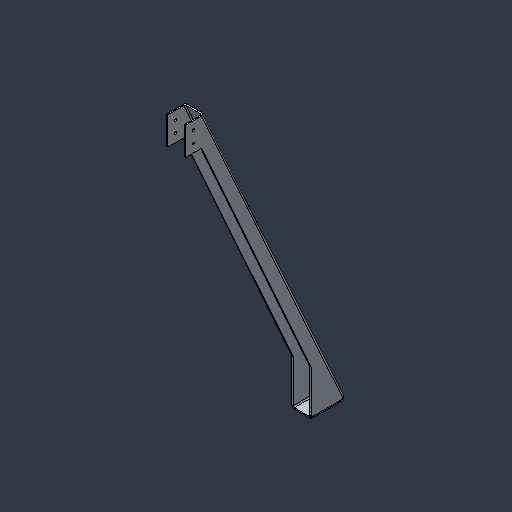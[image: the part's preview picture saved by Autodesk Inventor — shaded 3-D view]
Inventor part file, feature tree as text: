
AUTODESK INVENTOR PART (.ipt)
format: ipt  version: 2024.3 (Build 283343000, 343)  size: 129,536 bytes
history: native  units: mm (DEFAULTED — no unit token found)
features: fillet x1
ambient origin geometry x8: Origin, YZ Plane, XZ Plane, XY Plane, X Axis, Y Axis, Z Axis, Center Point
bodies: Solid1 (feature_tree)
feature tree (1):
  fillet  "Fillet1"  [1 undecoded]
note: 1 required parameter value undecoded (feature->parameter linkage not recoverable at this tier; creation-order binding heuristic only, values carry confidence <= 0.55)
